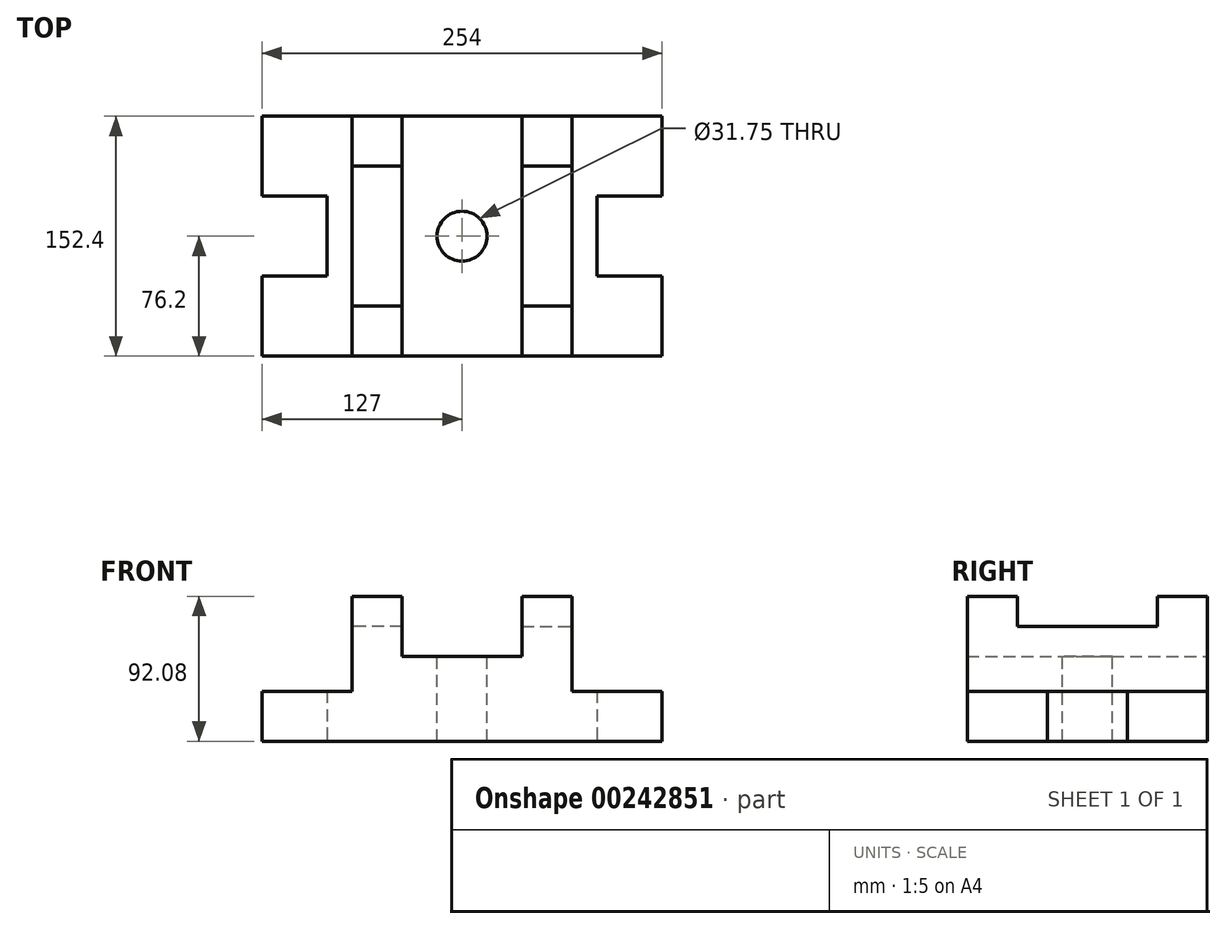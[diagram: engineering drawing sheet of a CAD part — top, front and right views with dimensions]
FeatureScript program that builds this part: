
annotation { "Feature Type Name" : "Feature", "Feature Type Description" : "" }
export const myFeature = defineFeature(function(context is Context, id is Id, definition is map)
    precondition{}
    {
        {
            var Q0;
            Q0=qCreatedBy(makeId("Front.planeOp"),FACE);
            var sketch = newSketch(context, id + "F0", { "sketchPlane" : qUnion([Q0])});
            skLineSegment(sketch, "E0", {"start": v(127, -83.73) * mm, "end": v(-127, -83.73) * mm});
            skLineSegment(sketch, "E1", {"start": v(-127, -83.73) * mm, "end": v(-127, -51.98) * mm});
            skLineSegment(sketch, "E2", {"start": v(-127, -51.98) * mm, "end": v(-69.85, -51.98) * mm});
            skLineSegment(sketch, "E3", {"start": v(127, -83.73) * mm, "end": v(127, -51.98) * mm});
            skLineSegment(sketch, "E4", {"start": v(127, -51.98) * mm, "end": v(69.85, -51.98) * mm});
            skLineSegment(sketch, "E5", {"start": v(-69.85, -51.98) * mm, "end": v(-69.85, 8.35) * mm});
            skLineSegment(sketch, "E6", {"start": v(69.85, -51.98) * mm, "end": v(69.85, 8.35) * mm});
            skLineSegment(sketch, "E7", {"start": v(-69.85, 8.35) * mm, "end": v(-38.1, 8.35) * mm});
            skLineSegment(sketch, "E8", {"start": v(69.85, 8.35) * mm, "end": v(38.1, 8.35) * mm});
            skLineSegment(sketch, "E9", {"start": v(-38.1, 8.35) * mm, "end": v(-38.1, -29.75) * mm});
            skLineSegment(sketch, "E10", {"start": v(38.1, 8.35) * mm, "end": v(38.1, -29.75) * mm});
            skLineSegment(sketch, "E11", {"start": v(-38.1, -29.75) * mm, "end": v(38.1, -29.75) * mm});
            skSolve(sketch);
        }
        {
            var Q0;
            Q0=makeQuery(id+"F0.imprint","IMPRINT",FACE,{"disambiguationData":[TD([[makeQuery(id+"F0.imprint","IMPRINT",EDGE,{"derivedFrom":sQuery(id+"F0.wireOp",EDGE,"E0")}),-1.0]])]});
            extrude(context, id + "F1", {"entities" : qUnion([Q0]), "depth" : 152.4 * mm});
        }
        {
            var Q0;
            Q0=makeQuery(id+"F1.opExtrude","SWEPT_FACE",FACE,{"disambiguationData":[OSD([sQuery(id+"F0.wireOp",EDGE,"E6")])]});
            var sketch = newSketch(context, id + "F2", { "sketchPlane" : qUnion([Q0])});
            skLineSegment(sketch, "E12", {"start": v(-152.4, -83.73) * mm, "end": v(-101.6, -83.73) * mm});
            skLineSegment(sketch, "E13", {"start": v(-101.6, -83.73) * mm, "end": v(-50.8, -83.73) * mm});
            skLineSegment(sketch, "E14", {"start": v(-50.8, -83.73) * mm, "end": v(0, -83.73) * mm});
            skLineSegment(sketch, "E15", {"start": v(-50.8, -83.73) * mm, "end": v(-50.8, -51.98) * mm});
            skLineSegment(sketch, "E16", {"start": v(-101.6, -83.73) * mm, "end": v(-101.6, -51.98) * mm});
            skLineSegment(sketch, "E17", {"start": v(-152.4, 8.35) * mm, "end": v(-120.65, 8.35) * mm});
            skLineSegment(sketch, "E18", {"start": v(0, 8.35) * mm, "end": v(-31.75, 8.35) * mm});
            skLineSegment(sketch, "E19", {"start": v(-120.65, 8.35) * mm, "end": v(-120.65, -10.7) * mm});
            skLineSegment(sketch, "E20", {"start": v(-31.75, 8.35) * mm, "end": v(-31.75, -10.7) * mm});
            skLineSegment(sketch, "E21", {"start": v(-31.75, -10.7) * mm, "end": v(-120.65, -10.7) * mm});
            skSolve(sketch);
        }
        {
            var Q0;
            Q0=makeQuery(id+"F1.opExtrude","SWEPT_FACE",FACE,{"disambiguationData":[OSD([sQuery(id+"F0.wireOp",EDGE,"E0")])]});
            var sketch = newSketch(context, id + "F3", { "sketchPlane" : qUnion([Q0])});
            skLineSegment(sketch, "E22", {"start": v(127, 0) * mm, "end": v(127, 50.8) * mm});
            skLineSegment(sketch, "E23", {"start": v(127, 50.8) * mm, "end": v(127, 101.6) * mm});
            skLineSegment(sketch, "E24", {"start": v(127, 101.6) * mm, "end": v(85.72, 101.6) * mm});
            skLineSegment(sketch, "E25", {"start": v(85.72, 101.6) * mm, "end": v(85.72, 50.8) * mm});
            skLineSegment(sketch, "E26", {"start": v(85.72, 50.8) * mm, "end": v(127, 50.8) * mm});
            skLineSegment(sketch, "E27", {"start": v(-127, 0) * mm, "end": v(-127, 50.8) * mm});
            skLineSegment(sketch, "E28", {"start": v(-127, 50.8) * mm, "end": v(-127, 101.6) * mm});
            skLineSegment(sketch, "E29", {"start": v(-127, 50.8) * mm, "end": v(-85.72, 50.8) * mm});
            skLineSegment(sketch, "E30", {"start": v(-85.72, 50.8) * mm, "end": v(-85.72, 101.6) * mm});
            skLineSegment(sketch, "E31", {"start": v(-85.72, 101.6) * mm, "end": v(-127, 101.6) * mm});
            skSolve(sketch);
        }
        {
            var Q0;
            Q0=makeQuery(id+"F3.imprint","IMPRINT",FACE,{"disambiguationData":[TD([[makeQuery(id+"F3.imprint","IMPRINT",EDGE,{"derivedFrom":sQuery(id+"F3.wireOp",EDGE,"E23")}),-1.0]])]});
            var Q1;
            Q1=makeQuery(id+"F3.imprint","IMPRINT",FACE,{"disambiguationData":[TD([[makeQuery(id+"F3.imprint","IMPRINT",EDGE,{"derivedFrom":sQuery(id+"F3.wireOp",EDGE,"E28")}),1.0]])]});
            extrude(context, id + "F4", {"entities" : qUnion([Q0, Q1]), "operationType" : NewBodyOperationType.REMOVE, "oppositeDirection" : true, "depth" : 31.75 * mm});
        }
        {
            var Q0;
            {var subQ0=sQuery(id+"F2.wireOp",EDGE,"E19");Q0=makeQuery(id+"F2.imprint","IMPRINT",FACE,{"disambiguationData":[TD([[makeQuery(id+"F2.imprint","IMPRINT",EDGE,{"derivedFrom":subQ0}),1.0]])]});}
            extrude(context, id + "F5", {"entities" : qUnion([Q0]), "operationType" : NewBodyOperationType.REMOVE, "oppositeDirection" : true, "depth" : 31.75 * mm});
        }
        {
            var Q0;
            Q0=makeQuery(id+"F1.opExtrude","SWEPT_FACE",FACE,{"disambiguationData":[OSD([sQuery(id+"F0.wireOp",EDGE,"E5")])]});
            var sketch = newSketch(context, id + "F6", { "sketchPlane" : qUnion([Q0])});
            skLineSegment(sketch, "E32", {"start": v(0, 8.35) * mm, "end": v(31.75, 8.35) * mm});
            skLineSegment(sketch, "E33", {"start": v(152.4, 8.35) * mm, "end": v(120.65, 8.35) * mm});
            skLineSegment(sketch, "E34", {"start": v(31.75, 8.35) * mm, "end": v(31.75, -10.7) * mm});
            skLineSegment(sketch, "E35", {"start": v(120.65, 8.35) * mm, "end": v(120.65, -10.7) * mm});
            skLineSegment(sketch, "E36", {"start": v(31.75, -10.7) * mm, "end": v(120.65, -10.7) * mm});
            skSolve(sketch);
        }
        {
            var Q0;
            {var subQ0=sQuery(id+"F6.wireOp",EDGE,"E34");Q0=makeQuery(id+"F6.imprint","IMPRINT",FACE,{"disambiguationData":[TD([[makeQuery(id+"F6.imprint","IMPRINT",EDGE,{"derivedFrom":subQ0}),1.0]])]});}
            extrude(context, id + "F7", {"entities" : qUnion([Q0]), "operationType" : NewBodyOperationType.REMOVE, "oppositeDirection" : true, "depth" : 31.75 * mm});
        }
        {
            var Q0;
            Q0=makeQuery(id+"F1.opExtrude","SWEPT_FACE",FACE,{"disambiguationData":[OSD([sQuery(id+"F0.wireOp",EDGE,"E11")])]});
            var sketch = newSketch(context, id + "F8", { "sketchPlane" : qUnion([Q0])});
            skCircle(sketch, "E37", {"center": v(0, -76.2) * mm, "radius": 15.88 * mm});
            skSolve(sketch);
        }
        {
            var Q0;
            Q0=makeQuery(id+"F8.imprint","IMPRINT",FACE,{"disambiguationData":[TD([[makeQuery(id+"F8.imprint","IMPRINT",EDGE,{"derivedFrom":sQuery(id+"F8.wireOp",EDGE,"E37")}),1.0]])]});
            extrude(context, id + "F9", {"entities" : qUnion([Q0]), "operationType" : NewBodyOperationType.REMOVE, "depth" : 254 * mm});
        }
        {
            var Q0;
            Q0 = qSketchRegion(id + "F8", true);
            extrude(context, id + "F10", {"entities" : qUnion([Q0]), "operationType" : NewBodyOperationType.REMOVE, "oppositeDirection" : true, "depth" : 254 * mm});
        }
    });
